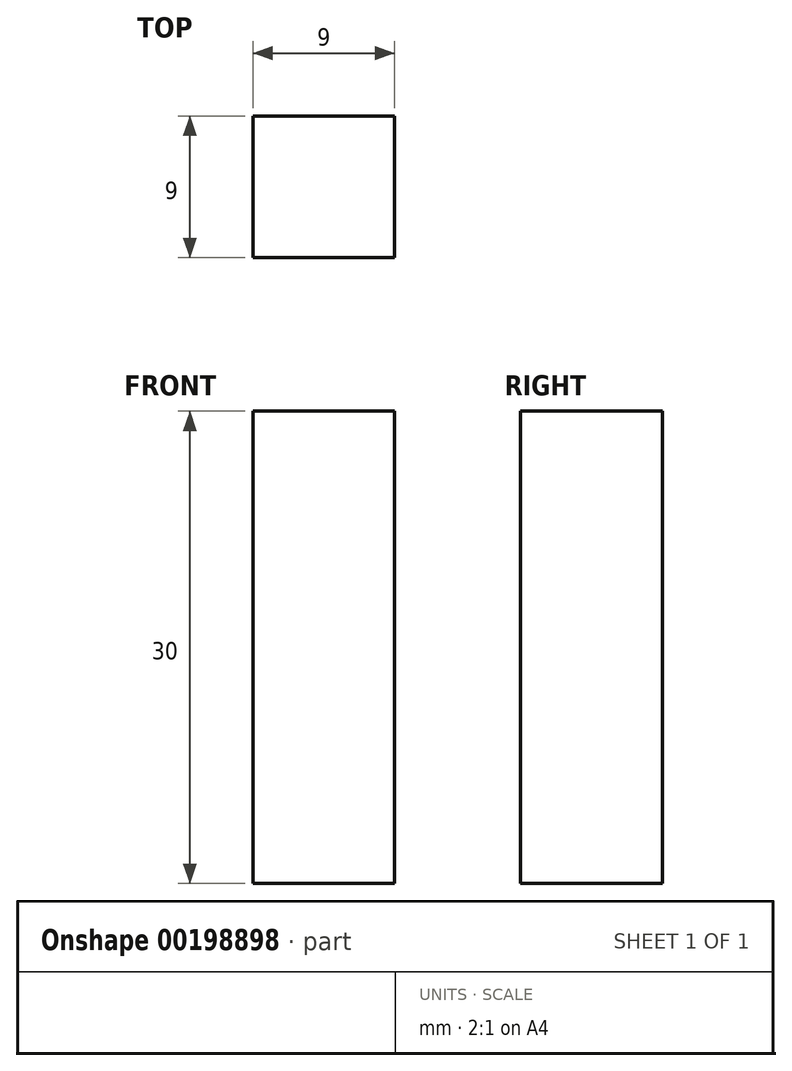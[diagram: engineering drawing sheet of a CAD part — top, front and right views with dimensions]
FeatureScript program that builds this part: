
annotation { "Feature Type Name" : "Feature", "Feature Type Description" : "" }
export const myFeature = defineFeature(function(context is Context, id is Id, definition is map)
    precondition{}
    {
        {
            var Q0;
            Q0=qCreatedBy(makeId("Top.planeOp"),FACE);
            var sketch = newSketch(context, id + "F0", { "sketchPlane" : qUnion([Q0])});
            skLineSegment(sketch, "E0.bottom", {"start": v(4.5, 4.5) * mm, "end": v(-4.5, 4.5) * mm});
            skLineSegment(sketch, "E0.top", {"start": v(4.5, -4.5) * mm, "end": v(-4.5, -4.5) * mm});
            skLineSegment(sketch, "E0.left", {"start": v(4.5, 4.5) * mm, "end": v(4.5, -4.5) * mm});
            skLineSegment(sketch, "E0.right", {"start": v(-4.5, 4.5) * mm, "end": v(-4.5, -4.5) * mm});
            skPoint(sketch, "E0.middle", {"position": v(0, 0) * mm});
            skSolve(sketch);
        }
        {
            var Q0;
            Q0=makeQuery(id+"F0.imprint","IMPRINT",FACE,{"disambiguationData":[TD([[makeQuery(id+"F0.imprint","IMPRINT",EDGE,{"derivedFrom":sQuery(id+"F0.wireOp",EDGE,"E0.bottom")}),1.0]])]});
            extrude(context, id + "F1", {"entities" : qUnion([Q0]), "depth" : 30 * mm});
        }
    });
